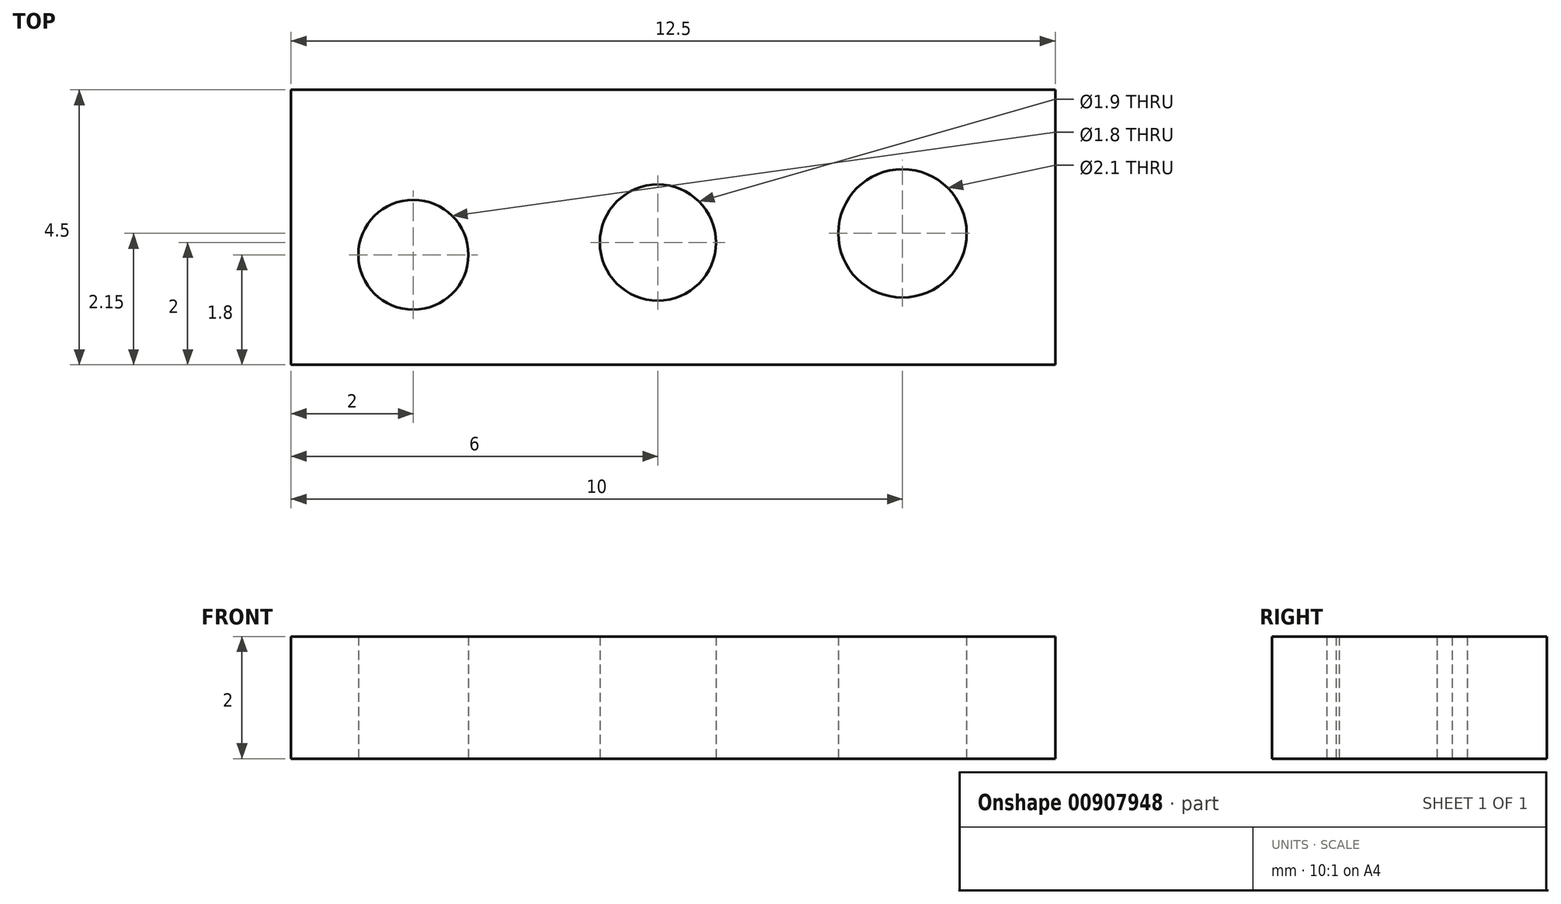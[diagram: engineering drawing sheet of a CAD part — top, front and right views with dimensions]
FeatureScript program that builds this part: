
annotation { "Feature Type Name" : "Feature", "Feature Type Description" : "" }
export const myFeature = defineFeature(function(context is Context, id is Id, definition is map)
    precondition{}
    {
        {
            var Q0;
            Q0=qCreatedBy(makeId("Top.planeOp"),FACE);
            var sketch = newSketch(context, id + "F0", { "sketchPlane" : qUnion([Q0])});
            skLineSegment(sketch, "E0.bottom", {"start": v(-6.25, 2.25) * mm, "end": v(6.25, 2.25) * mm});
            skLineSegment(sketch, "E0.top", {"start": v(-6.25, -2.25) * mm, "end": v(6.25, -2.25) * mm});
            skLineSegment(sketch, "E0.left", {"start": v(-6.25, 2.25) * mm, "end": v(-6.25, -2.25) * mm});
            skLineSegment(sketch, "E0.right", {"start": v(6.25, 2.25) * mm, "end": v(6.25, -2.25) * mm});
            skPoint(sketch, "E0.middle", {"position": v(0, 0) * mm});
            skLineSegment(sketch, "E1", {"start": v(-6.25, -2.25) * mm, "end": v(-4.25, -2.25) * mm});
            skLineSegment(sketch, "E2", {"start": v(-4.25, -2.25) * mm, "end": v(-4.25, -0.45) * mm});
            skCircle(sketch, "E3", {"center": v(-4.25, -0.45) * mm, "radius": 0.9 * mm});
            skLineSegment(sketch, "E4", {"start": v(-4.25, -2.25) * mm, "end": v(-0.25, -2.25) * mm});
            skLineSegment(sketch, "E5", {"start": v(-0.25, -2.25) * mm, "end": v(-0.25, -0.25) * mm});
            skCircle(sketch, "E6", {"center": v(-0.25, -0.25) * mm, "radius": 0.95 * mm});
            skLineSegment(sketch, "E7", {"start": v(-0.25, -2.25) * mm, "end": v(3.75, -2.25) * mm});
            skLineSegment(sketch, "E8", {"start": v(-0.25, -1.25) * mm, "end": v(-0.25, -2.25) * mm});
            skLineSegment(sketch, "E9", {"start": v(-4.25, -1.35) * mm, "end": v(-4.25, -2.25) * mm});
            skPoint(sketch, "E10.center.orphan", {"position": v(3.75, -0.1) * mm});
            skCircle(sketch, "E11", {"center": v(3.75, -0.1) * mm, "radius": 1.05 * mm});
            skLineSegment(sketch, "E12", {"start": v(3.75, -1.15) * mm, "end": v(3.75, -2.25) * mm});
            skSolve(sketch);
        }
        {
            var Q0;
            Q0 = qSketchRegion(id + "F0", true);
            extrude(context, id + "F1", {"entities" : qUnion([Q0]), "depth" : 2 * mm, "offsetDistance" : 25 * mm});
        }
    });
